# Revit family: Range_Hood-BroanNutone-Convertible-Under_Cabinet-30in-BCDF130SS
name_source: partatom
category: Specialty Equipment
units: mm (PartAtom-declared; Revit-internal decimal feet)

## family parameters
Cut with Voids When Loaded = No
Host = Face
OmniClass Number = 23.40.20.34.11.21
OmniClass Title = Fireplace and Stove Hoods
Part Type = Normal
Room Calculation Point = No
Round Connector Dimension = Use Diameter
Shared = No

## types (2) — shared parameters
Apparent Load = 0 VA
Assembly Code = E1090320
Depth = 1' - 7 5/8"
Description = 30-Inch Convertible Under-Cabinet Range Hood, 375 Max Blower
Electrical Connector = Cord Kit - Standard 120 VAC Plug
Height = 0' - 6"
Manufacturer = Broan-NuTone
Model = BCDF130SS
Mounting Note = For best results mount 24 to 30 inches over cooking surface
Number of Poles = 1
Power Factor = 1
Product Documentation Link = https://www.broan-nutone.com
Product Name = Broan® Glacier 30-Inch Convertible Under-Cabinet Range Hood, 375 Max Blower CFM, Black Stainless Steel
Product Page URL = https://www.broan-nutone.com
URL = https://www.broan-nutone.com
Version = 2019 – v1.0a
Voltage = 120 V
Voltage Note = 120 V
Warranty URL = https://www.broan-nutone.com
Width = 2' - 5 7/8"

## per-type parameters (varying)
| type | Default Elevation | Finish |
| 30" Stainless Steel | 4' - 0" | Metal - Broan NuTone - Stainless Steel |
| 30" Black Stainless Steel | 2' - 0" | Metal - Broan NuTone - Stainless Steel - Black |

## geometry (parser evidence)
native form markers: Sweep x3
no freeform markers — native parametric forms only
